# Revit family: UCV-S
name_source: partatom
category: Mechanical Equipment
units: mm (PartAtom-declared; Revit-internal decimal feet)

## family parameters
Always vertical = Yes
Cut with Voids When Loaded = No
Part Type = Normal
Room Calculation Point = No
Round Connector Dimension = Use Diameter
Shared = No
Work Plane-Based = No

## types (9) — shared parameters
0 = 0' - 0"
1" = 0' - 1"
1.5 = 0' - 1 1/2"
2" = 0' - 2"
2' = 2' - 0"
3" = 0' - 3"
4" = 0' - 4"
Manufacturer = Loren Cook Company
Model = UCV-S
ONE EIGTH = 0' - 0 1/8"
Type Comments = Upblast Centri-Vane Stretch All Aluminum Inline Centrifugal Blower Roof Mounted/Belt Drive
URL = www.lorencook.com

## per-type parameters (varying)
- 12_UCV-S: (C/2)+B=2' - 0 23/32"; (T_SQ/2)+.125"=0' - 10 1/8"; -B/2=-0' - 7 1/2"; -C*.3=-0' - 5 27/32"; A=2' - 8 7/8"; A/2=1' - 4 7/16"; A/3=0' - 10 31/32"; B=1' - 3"; B/2=0' - 7 1/2"; C=1' - 7 7/16"; C*.3=0' - 5 27/32"; C/2=0' - 9 23/32"; D=0' - 8"; E=3' - 4 7/8"; F=1' - 4"; F/2=0' - 8"; G=0' - 2"; G-.125"=0' - 1 7/8"; L=0' - 1"; M=1' - 2 5/8"; M/2=0' - 7 5/16"; N=1' - 0"; N/2=0' - 6"; RO=1' - 3 1/2"; RO/2=0' - 7 3/4"; T_SQ=1' - 8"; T_SQ/2=0' - 10"
- 14_UCV-S: (C/2)+B=2' - 3 3/32"; (T_SQ/2)+.125"=1' - 0 1/8"; -B/2=-0' - 8"; -C*.3=-0' - 6 21/32"; A=3' - 0"; A/2=1' - 6"; A/3=1' - 0"; B=1' - 4"; B/2=0' - 8"; C=1' - 10 3/16"; C*.3=0' - 6 21/32"; C/2=0' - 11 3/32"; D=0' - 10"; E=3' - 10"; F=1' - 6"; F/2=0' - 9"; G=0' - 2"; G-.125"=0' - 1 7/8"; L=0' - 1"; M=1' - 4 5/8"; M/2=0' - 8 5/16"; N=1' - 2"; N/2=0' - 7"; RO=1' - 7 1/2"; RO/2=0' - 9 3/4"; T_SQ=2' - 0"; T_SQ/2=1' - 0"
- 16_UCV-S: (C/2)+B=2' - 5 25/32"; (T_SQ/2)+.125"=1' - 2 1/8"; -B/2=-0' - 8 1/2"; -C*.3=-0' - 7 21/32"; A=3' - 3 9/16"; A/2=1' - 7 25/32"; A/3=1' - 1 3/16"; B=1' - 5"; B/2=0' - 8 1/2"; C=2' - 1 9/16"; C*.3=0' - 7 21/32"; C/2=1' - 0 25/32"; D=0' - 10"; E=4' - 1 9/16"; F=1' - 9"; F/2=0' - 10 1/2"; G=0' - 2"; G-.125"=0' - 1 7/8"; L=0' - 1"; M=1' - 6 5/8"; M/2=0' - 9 5/16"; N=1' - 4"; N/2=0' - 8"; RO=1' - 11 1/2"; RO/2=0' - 11 3/4"; T_SQ=2' - 4"; T_SQ/2=1' - 2"
- 18_UCV-S: (C/2)+B=2' - 9 7/32"; (T_SQ/2)+.125"=1' - 4 1/8"; -B/2=-0' - 9 1/2"; -C*.3=-0' - 8 17/32"; A=3' - 7 5/8"; A/2=1' - 9 13/16"; A/3=1' - 2 17/32"; B=1' - 7"; B/2=0' - 9 1/2"; C=2' - 4 7/16"; C*.3=0' - 8 17/32"; C/2=1' - 2 7/32"; D=1' - 0"; E=4' - 7 5/8"; F=1' - 11"; F/2=0' - 11 1/2"; G=0' - 2"; G-.125"=0' - 1 7/8"; L=0' - 1"; M=1' - 8 5/8"; M/2=0' - 10 5/16"; N=1' - 6"; N/2=0' - 9"; RO=2' - 3 1/2"; RO/2=1' - 1 3/4"; T_SQ=2' - 8"; T_SQ/2=1' - 4"
- 20_UCV-S: (C/2)+B=2' - 10 19/32"; (T_SQ/2)+.125"=1' - 4 1/8"; -B/2=-0' - 9 1/2"; -C*.3=-0' - 9 11/32"; A=3' - 10 5/8"; A/2=1' - 11 5/16"; A/3=1' - 3 17/32"; B=1' - 7"; B/2=0' - 9 1/2"; C=2' - 7 3/16"; C*.3=0' - 9 11/32"; C/2=1' - 3 19/32"; D=1' - 0"; E=4' - 10 5/8"; F=2' - 1"; F/2=1' - 0 1/2"; G=0' - 2"; G-.125"=0' - 1 7/8"; L=0' - 1"; M=1' - 10 5/8"; M/2=0' - 11 5/16"; N=1' - 8"; N/2=0' - 10"; RO=2' - 3 1/2"; RO/2=1' - 1 3/4"; T_SQ=2' - 8"; T_SQ/2=1' - 4"
- 24_UCV-S: (C/2)+B=3' - 3 25/32"; (T_SQ/2)+.125"=1' - 6 1/8"; -B/2=-0' - 10 1/2"; -C*.3=-0' - 11 9/32"; A=4' - 5 3/4"; A/2=2' - 2 7/8"; A/3=1' - 5 29/32"; B=1' - 9"; B/2=0' - 10 1/2"; C=3' - 1 9/16"; C*.3=0' - 11 9/32"; C/2=1' - 6 25/32"; D=1' - 2"; E=5' - 7 3/4"; F=2' - 5"; F/2=1' - 2 1/2"; G=0' - 3"; G-.125"=0' - 2 7/8"; L=0' - 1 3/16"; M=2' - 3 1/8"; M/2=1' - 1 9/16"; N=2' - 0"; N/2=1' - 0"; RO=2' - 7 1/2"; RO/2=1' - 3 3/4"; T_SQ=3' - 0"; T_SQ/2=1' - 6"
- 28_UCV-S: (C/2)+B=4' - 2 17/32"; (T_SQ/2)+.125"=1' - 9 1/8"; -B/2=-1' - 2 1/2"; -C*.3=-1' - 0 29/32"; A=5' - 0 3/4"; A/2=2' - 6 3/8"; A/3=1' - 8 1/4"; B=2' - 5"; B/2=1' - 2 1/2"; C=3' - 7 1/16"; C*.3=1' - 0 29/32"; C/2=1' - 9 17/32"; D=1' - 4"; E=6' - 4 3/4"; F=2' - 9"; F/2=1' - 4 1/2"; G=0' - 3"; G-.125"=0' - 2 7/8"; L=0' - 1 3/16"; M=2' - 7 1/8"; M/2=1' - 3 9/16"; N=2' - 4"; N/2=1' - 2"; RO=3' - 1 1/2"; RO/2=1' - 6 3/4"; T_SQ=3' - 6"; T_SQ/2=1' - 9"
- 32_UCV-S: (C/2)+B=4' - 6 15/32"; (T_SQ/2)+.125"=2' - 0 1/8"; -B/2=-1' - 3"; -C*.3=-1' - 2 11/16"; A=5' - 7 7/8"; A/2=2' - 9 15/16"; A/3=1' - 10 5/8"; B=2' - 6"; B/2=1' - 3"; C=4' - 0 15/16"; C*.3=1' - 2 11/16"; C/2=2' - 0 15/32"; D=1' - 6"; E=7' - 1 7/8"; F=3' - 1"; F/2=1' - 6 1/2"; G=0' - 3"; G-.125"=0' - 2 7/8"; L=0' - 1 7/16"; M=2' - 11 1/8"; M/2=1' - 5 9/16"; N=2' - 8"; N/2=1' - 4"; RO=3' - 7 1/2"; RO/2=1' - 9 3/4"; T_SQ=4' - 0"; T_SQ/2=2' - 0"
- 36_UCV-S: (C/2)+B=4' - 11 5/16"; (T_SQ/2)+.125"=2' - 3 1/8"; -B/2=-1' - 4"; -C*.3=-1' - 4 3/8"; A=6' - 1 1/2"; A/2=3' - 0 3/4"; A/3=2' - 0 1/2"; B=2' - 8"; B/2=1' - 4"; C=4' - 6 5/8"; C*.3=1' - 4 3/8"; C/2=2' - 3 5/16"; D=1' - 8"; E=7' - 9 1/2"; F=3' - 5"; F/2=1' - 8 1/2"; G=0' - 3"; G-.125"=0' - 2 7/8"; L=0' - 1 15/16"; M=3' - 3 1/8"; M/2=1' - 7 9/16"; N=3' - 0"; N/2=1' - 6"; RO=4' - 1 1/2"; RO/2=2' - 0 3/4"; T_SQ=4' - 6"; T_SQ/2=2' - 3"

## geometry (parser evidence)
native form markers: Sweep x2
no freeform markers — native parametric forms only
